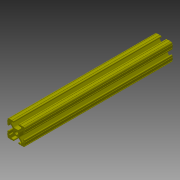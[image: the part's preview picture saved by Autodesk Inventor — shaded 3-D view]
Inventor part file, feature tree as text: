
AUTODESK INVENTOR PART (.ipt)
format: ipt  version: 2014 SP2 (Build 180246200, 246)  size: 199,680 bytes
history: native  units: in
note: dims shown in document units (in); Inventor stores cm internally (conversion verified against a paired STEP export)
features: other x21, extrude x1, sketch x1
ambient origin geometry x8: Origin, YZ Plane, XZ Plane, XY Plane, X Axis, Y Axis, Z Axis, Center Point
bodies: Solid1 (feature_tree)
feature tree (23):
  extrude  "Extrusion1"  [1 undecoded]
  other  "b1_XY"
  other  "b1_YZ"
  other  "b1_ZX"
  other  "b1_X"
  other  "b1_Y"
  other  "b1_Z"
  other  "b1_Center"
  other  "b2_XY"
  other  "b2_YZ"
  other  "b2_ZX"
  other  "b2_X"
  other  "b2_Y"
  other  "b2_Z"
  other  "b2_Center"
  other  "profile1010_XY"
  other  "profile1010_YZ"
  other  "profile1010_ZX"
  other  "profile1010_X"
  other  "profile1010_Y"
  other  "profile1010_Z"
  other  "profile1010_Center"
  sketch  "Sketch_1"  dims[d0=8.5in d1=0.0in]
note: 1 required parameter value undecoded (feature->parameter linkage not recoverable at this tier; creation-order binding heuristic only, values carry confidence <= 0.55)
